# Revit family: DOWNLIGHT DISH_D24012SW.1
name_source: partatom
category: Luminarias
units: mm (PartAtom-declared; Revit-internal decimal feet)

## family parameters
Compartido = No
Corte con vacíos al cargar = No
Cota de conector redondo = Diámetro de uso
Origen de luz = Sí
Punto de cálculo de habitación = No
Se basa en plano de trabajo = Sí
Siempre vertical = Sí
Tipo de pieza = Normal

## types (3) — shared parameters
Cambio de temperatura de color de luz atenuada = <Ninguno>
Comentarios de vataje = 90-240V
Elevación por defecto = 1219 mm
Fabricante = BRILLANT
Filtro de color = 16777215
Longitud de símbolo de origen de luz = 500 mm  [stored 1.64042 ft]
Lámpara = EPSITAR
Watt per fixture = 9
Ángulo de campo de foco = 120.00°
Ángulo de enfoque = 120.00°
Ángulo de inclinación = 60.00°

## per-type parameters (varying)
| type | Descripción | Modelo |
| DOWNLIGHT DISH_D24012SW.1 | LUMINARIA TIPO CIRCULAR PARA EMPOTRAR EN TECHO CON CUERPO DE ALUMINIO Y VIDRIO SATINADO, IP 33 USO PARA INTERIORES, CUENTA CON 1 LED TIPO EPISTAR CON UNA POTENCIA TOTAL DE 9W, A UNA TEMPERATURA EN BLANCO CALIDO 3000K CON 750 LUMENES, EFICIENCIA DE 83.33LM/W, IRC 80, APERTURA A 120 GRADOS EN STOCK, CON FUENTE EXTERNA REMOTA (INCLUIDA) ALIMENTADA A 90-240V. | D24012SW.1 |
| DOWNLIGHT DISH_D24012SW.2 | LUMINARIA TIPO CIRCULAR PARA EMPOTRAR EN TECHO CON CUERPO DE ALUMINIO Y VIDRIO SATINADO, IP 33 USO PARA INTERIORES, CUENTA CON 1 LED TIPO EPISTAR CON UNA POTENCIA TOTAL DE 9W, A UNA TEMPERATURA EN BLANCO CALIDO 3000K CON 750 LUMENES, EFICIENCIA DE 83.33LM/W, IRC 80, APERTURA A 120 GRADOS EN STOCK, CON FUENTE EXTERNA REMOTA (INCLUIDA) ALIMENTADA A 90-240V. DIMEABLE (OPCIONAL) | D24012SW.2 |
| DOWNLIGHT DISH_D24012SN.1 | LUMINARIA TIPO CIRCULAR PARA EMPOTRAR EN TECHO CON CUERPO DE ALUMINIO Y VIDRIO SATINADO, IP 33 USO PARA INTERIORES, CUENTA CON 1 LED TIPO EPISTAR CON UNA POTENCIA TOTAL DE 9W, A UNA TEMPERATURA EN BLANCO FRIO 4500K CON 750 LUMENES, EFICIENCIA DE 83.33LM/W, IRC 80, APERTURA A 120 GRADOS EN STOCK, CON FUENTE EXTERNA REMOTA (INCLUIDA) ALIMENTADA A 90-240V. DIMEABLE (OPCIONAL) | D24012SN.1 |

note: [stored X ft] marks values corroborated as IEEE doubles in the binary element streams (Revit-internal decimal feet)

## geometry (parser evidence)
native form markers: Blend x2
no freeform markers — native parametric forms only
